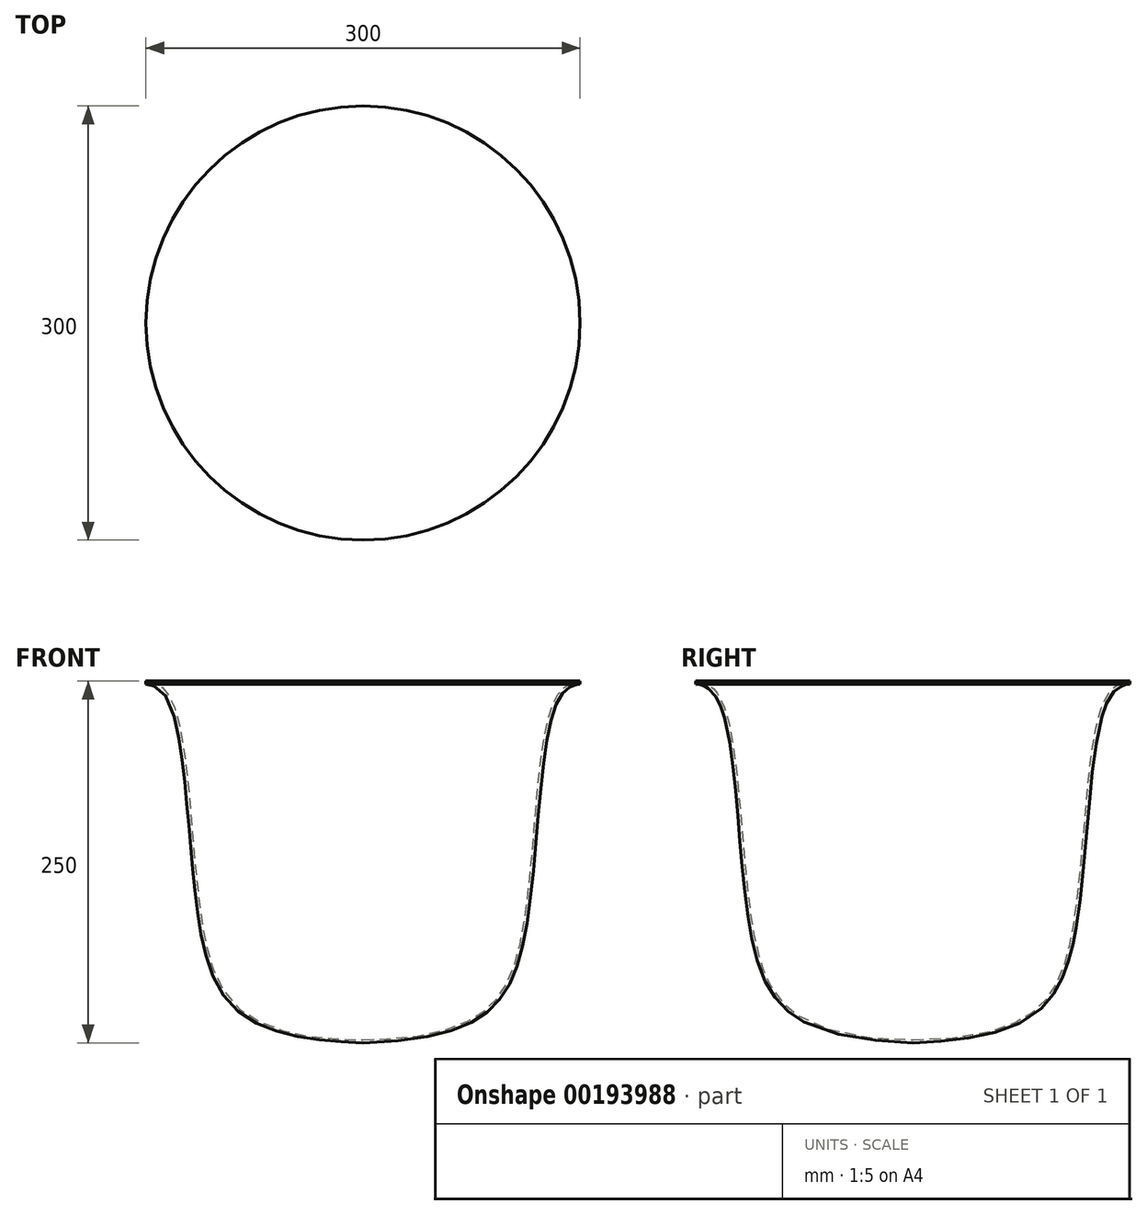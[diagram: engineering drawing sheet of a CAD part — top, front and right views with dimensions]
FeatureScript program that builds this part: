
annotation { "Feature Type Name" : "Feature", "Feature Type Description" : "" }
export const myFeature = defineFeature(function(context is Context, id is Id, definition is map)
    precondition{}
    {
        {
            var Q0;
            Q0=qCreatedBy(makeId("Front.planeOp"),FACE);
            var sketch = newSketch(context, id + "F0", { "sketchPlane" : qUnion([Q0])});
            skLineSegment(sketch, "E0", {"start": v(0, 43.98) * mm, "end": v(0, -46) * mm});
            skFitSpline(sketch, "E1", {"points": [v(0, -157.05) * mm, v(111.25, -85.12) * mm, v(137.52, 84.25) * mm, v(150, 90.95) * mm], "startDerivative": vector(600.91, 20.67) * mm, "endDerivative": vector(23.01, 0) * mm});
            skFitSpline(sketch, "E2.0", {"points": [v(-0.07, -155.05) * mm, v(12.4, -154.63) * mm, v(34.41, -152.94) * mm, v(55.5, -148.58) * mm, v(69.05, -143.67) * mm, v(77.71, -139.26) * mm, v(85.02, -134.1) * mm, v(91.15, -128.15) * mm, v(96.27, -121.37) * mm, v(100.53, -113.68) * mm, v(104.04, -105.03) * mm, v(106.95, -95.4) * mm, v(109.38, -84.73) * mm, v(111.45, -73.03) * mm, v(113.23, -60.5) * mm, v(114.76, -47.34) * mm, v(116.12, -33.77) * mm, v(117.76, -15.37) * mm, v(119.67, 7.68) * mm, v(121.77, 29.47) * mm, v(123.83, 45.36) * mm, v(125.61, 56.32) * mm, v(127.71, 66.12) * mm, v(129.79, 73.19) * mm, v(131.69, 78.1) * mm, v(133.25, 81.38) * mm, v(134.68, 83.78) * mm, v(135.93, 85.48) * mm, v(137.24, 87.03) * mm, v(138.95, 88.65) * mm, v(141.74, 90.65) * mm, v(144.44, 91.86) * mm, v(146.74, 92.52) * mm, v(148.2, 92.8) * mm, v(149.14, 92.9) * mm, v(149.7, 92.94) * mm, v(149.9, 92.95) * mm, v(150, 92.95) * mm]});
            skLineSegment(sketch, "E3", {"start": v(150, 92.95) * mm, "end": v(150, 90.95) * mm});
            skLineSegment(sketch, "E4", {"start": v(0, -155.05) * mm, "end": v(0, -157.05) * mm});
            skSolve(sketch);
        }
        {
            var Q0;
            Q0=makeQuery(id+"F0.imprint","IMPRINT",FACE,{"disambiguationData":[TD([[makeQuery(id+"F0.imprint","IMPRINT",EDGE,{"derivedFrom":sQuery(id+"F0.wireOp",EDGE,"E1")}),1.0]])]});
            var Q1;
            Q1=sQuery(id+"F0.wireOp",EDGE,"E0");
            revolve(context, id + "F1", {"entities" : qUnion([Q0]), "axis" : qUnion([Q1]), "revolveType" : RevolveType.FULL});
        }
    });
